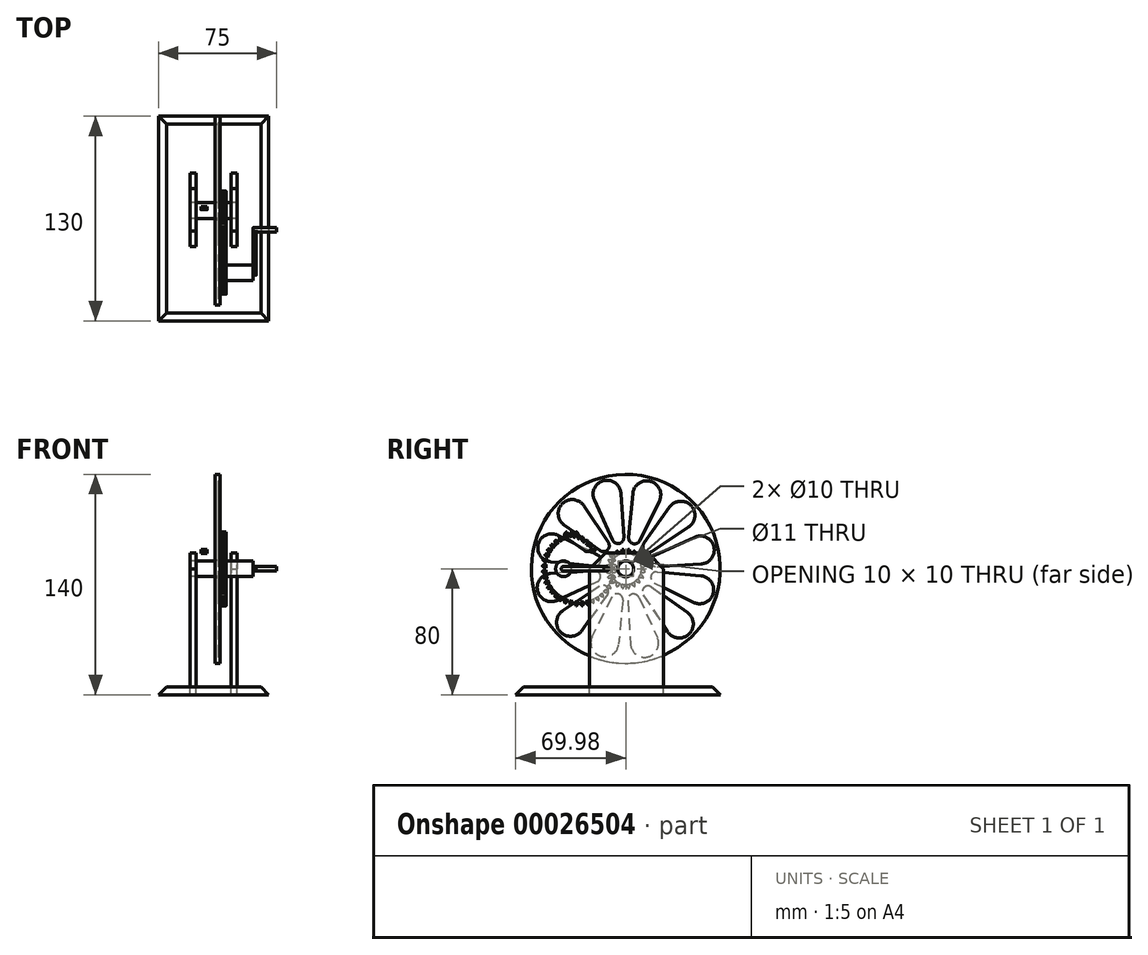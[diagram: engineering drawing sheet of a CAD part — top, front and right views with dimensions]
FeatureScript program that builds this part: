
annotation { "Feature Type Name" : "Feature", "Feature Type Description" : "" }
export const myFeature = defineFeature(function(context is Context, id is Id, definition is map)
    precondition{}
    {
        {
            var Q0;
            Q0=qCreatedBy(makeId("Right.planeOp"),FACE);
            var sketch = newSketch(context, id + "F0", { "sketchPlane" : qUnion([Q0])});
            skCircle(sketch, "E0", {"center": v(0, 0) * mm, "radius": 60 * mm});
            skLineSegment(sketch, "E1", {"start": v(1.87, 19.91) * mm, "end": v(4.48, 47.8) * mm});
            skLineSegment(sketch, "E2", {"start": v(8.88, 17.92) * mm, "end": v(21.32, 43) * mm});
            skCircle(sketch, "E3", {"center": v(0, 0) * mm, "radius": 5 * mm});
            skArc(sketch, "E4", {"start": v(1.87, 19.91) * mm, "mid": v(4.55, 16) * mm, "end": v(8.88, 17.92) * mm});
            skArc(sketch, "E5", {"start": v(4.48, 47.8) * mm, "mid": v(15.77, 55.52) * mm, "end": v(21.32, 43) * mm});
            skArc(sketch, "E6.1.0", {"start": v(-8.34, 18.18) * mm, "mid": v(-4.06, 16.13) * mm, "end": v(-1.27, 19.96) * mm});
            skArc(sketch, "E6.1.5", {"start": v(-20.01, 43.63) * mm, "mid": v(-14.1, 55.97) * mm, "end": v(-3.04, 47.9) * mm});
            skLineSegment(sketch, "E6.1.8", {"start": v(-1.27, 19.96) * mm, "end": v(-3.04, 47.9) * mm});
            skLineSegment(sketch, "E6.1.9", {"start": v(-8.34, 18.18) * mm, "end": v(-20.01, 43.63) * mm});
            skArc(sketch, "E6.2.0", {"start": v(-16.31, 11.57) * mm, "mid": v(-11.58, 11.94) * mm, "end": v(-11.08, 16.65) * mm});
            skArc(sketch, "E6.2.5", {"start": v(-39.15, 27.78) * mm, "mid": v(-40.2, 41.42) * mm, "end": v(-26.59, 39.96) * mm});
            skLineSegment(sketch, "E6.2.8", {"start": v(-11.08, 16.65) * mm, "end": v(-26.59, 39.96) * mm});
            skLineSegment(sketch, "E6.2.9", {"start": v(-16.31, 11.57) * mm, "end": v(-39.15, 27.78) * mm});
            skArc(sketch, "E6.3.0", {"start": v(-19.91, 1.87) * mm, "mid": v(-16, 4.55) * mm, "end": v(-17.92, 8.88) * mm});
            skArc(sketch, "E6.3.5", {"start": v(-47.8, 4.48) * mm, "mid": v(-55.52, 15.77) * mm, "end": v(-43, 21.32) * mm});
            skLineSegment(sketch, "E6.3.8", {"start": v(-17.92, 8.88) * mm, "end": v(-43, 21.32) * mm});
            skLineSegment(sketch, "E6.3.9", {"start": v(-19.91, 1.87) * mm, "end": v(-47.8, 4.48) * mm});
            skArc(sketch, "E6.4.0", {"start": v(-18.18, -8.34) * mm, "mid": v(-16.13, -4.06) * mm, "end": v(-19.96, -1.27) * mm});
            skArc(sketch, "E6.4.5", {"start": v(-43.63, -20.01) * mm, "mid": v(-55.97, -14.1) * mm, "end": v(-47.9, -3.04) * mm});
            skLineSegment(sketch, "E6.4.8", {"start": v(-19.96, -1.27) * mm, "end": v(-47.9, -3.04) * mm});
            skLineSegment(sketch, "E6.4.9", {"start": v(-18.18, -8.34) * mm, "end": v(-43.63, -20.01) * mm});
            skArc(sketch, "E6.5.0", {"start": v(-11.57, -16.31) * mm, "mid": v(-11.94, -11.58) * mm, "end": v(-16.65, -11.08) * mm});
            skArc(sketch, "E6.5.5", {"start": v(-27.78, -39.15) * mm, "mid": v(-41.42, -40.2) * mm, "end": v(-39.96, -26.59) * mm});
            skLineSegment(sketch, "E6.5.8", {"start": v(-16.65, -11.08) * mm, "end": v(-39.96, -26.59) * mm});
            skLineSegment(sketch, "E6.5.9", {"start": v(-11.57, -16.31) * mm, "end": v(-27.78, -39.15) * mm});
            skArc(sketch, "E6.6.0", {"start": v(-1.87, -19.91) * mm, "mid": v(-4.55, -16) * mm, "end": v(-8.88, -17.92) * mm});
            skArc(sketch, "E6.6.5", {"start": v(-4.48, -47.8) * mm, "mid": v(-15.77, -55.52) * mm, "end": v(-21.32, -43) * mm});
            skLineSegment(sketch, "E6.6.8", {"start": v(-8.88, -17.92) * mm, "end": v(-21.32, -43) * mm});
            skLineSegment(sketch, "E6.6.9", {"start": v(-1.87, -19.91) * mm, "end": v(-4.48, -47.8) * mm});
            skArc(sketch, "E6.7.0", {"start": v(8.34, -18.18) * mm, "mid": v(4.06, -16.13) * mm, "end": v(1.27, -19.96) * mm});
            skArc(sketch, "E6.7.5", {"start": v(20.01, -43.63) * mm, "mid": v(14.1, -55.97) * mm, "end": v(3.04, -47.9) * mm});
            skLineSegment(sketch, "E6.7.8", {"start": v(1.27, -19.96) * mm, "end": v(3.04, -47.9) * mm});
            skLineSegment(sketch, "E6.7.9", {"start": v(8.34, -18.18) * mm, "end": v(20.01, -43.63) * mm});
            skArc(sketch, "E6.8.0", {"start": v(16.31, -11.57) * mm, "mid": v(11.58, -11.94) * mm, "end": v(11.08, -16.65) * mm});
            skArc(sketch, "E6.8.5", {"start": v(39.15, -27.78) * mm, "mid": v(40.2, -41.42) * mm, "end": v(26.59, -39.96) * mm});
            skLineSegment(sketch, "E6.8.8", {"start": v(11.08, -16.65) * mm, "end": v(26.59, -39.96) * mm});
            skLineSegment(sketch, "E6.8.9", {"start": v(16.31, -11.57) * mm, "end": v(39.15, -27.78) * mm});
            skArc(sketch, "E6.9.0", {"start": v(19.91, -1.87) * mm, "mid": v(16, -4.55) * mm, "end": v(17.92, -8.88) * mm});
            skArc(sketch, "E6.9.5", {"start": v(47.8, -4.48) * mm, "mid": v(55.52, -15.77) * mm, "end": v(43, -21.32) * mm});
            skLineSegment(sketch, "E6.9.8", {"start": v(17.92, -8.88) * mm, "end": v(43, -21.32) * mm});
            skLineSegment(sketch, "E6.9.9", {"start": v(19.91, -1.87) * mm, "end": v(47.8, -4.48) * mm});
            skArc(sketch, "E6.10.0", {"start": v(18.18, 8.34) * mm, "mid": v(16.13, 4.06) * mm, "end": v(19.96, 1.27) * mm});
            skArc(sketch, "E6.10.5", {"start": v(43.63, 20.01) * mm, "mid": v(55.97, 14.1) * mm, "end": v(47.9, 3.04) * mm});
            skLineSegment(sketch, "E6.10.8", {"start": v(19.96, 1.27) * mm, "end": v(47.9, 3.04) * mm});
            skLineSegment(sketch, "E6.10.9", {"start": v(18.18, 8.34) * mm, "end": v(43.63, 20.01) * mm});
            skArc(sketch, "E6.11.0", {"start": v(11.57, 16.31) * mm, "mid": v(11.94, 11.58) * mm, "end": v(16.65, 11.08) * mm});
            skArc(sketch, "E6.11.5", {"start": v(27.78, 39.15) * mm, "mid": v(41.42, 40.2) * mm, "end": v(39.96, 26.59) * mm});
            skLineSegment(sketch, "E6.11.8", {"start": v(16.65, 11.08) * mm, "end": v(39.96, 26.59) * mm});
            skLineSegment(sketch, "E6.11.9", {"start": v(11.57, 16.31) * mm, "end": v(27.78, 39.15) * mm});
            skCircle(sketch, "E7", {"center": v(0, 0) * mm, "radius": 5.5 * mm});
            skSolve(sketch);
        }
        {
            var Q0;
            Q0=makeQuery(id+"F0.imprint","IMPRINT",FACE,{"disambiguationData":[TD([[makeQuery(id+"F0.imprint","IMPRINT",EDGE,{"derivedFrom":sQuery(id+"F0.wireOp",EDGE,"E0")}),1.0]])]});
            var Q1;
            Q1=makeQuery(id+"F0.imprint","IMPRINT",FACE,{"disambiguationData":[TD([[makeQuery(id+"F0.imprint","IMPRINT",EDGE,{"derivedFrom":sQuery(id+"F0.wireOp",EDGE,"E1")}),-1.0]])]});
            var Q2;
            Q2=makeQuery(id+"F0.imprint","IMPRINT",FACE,{"disambiguationData":[TD([[makeQuery(id+"F0.imprint","IMPRINT",EDGE,{"derivedFrom":sQuery(id+"F0.wireOp",EDGE,"E6.1.0")}),1.0]])]});
            var Q3;
            Q3=makeQuery(id+"F0.imprint","IMPRINT",FACE,{"disambiguationData":[TD([[makeQuery(id+"F0.imprint","IMPRINT",EDGE,{"derivedFrom":sQuery(id+"F0.wireOp",EDGE,"E6.2.0")}),1.0]])]});
            var Q4;
            Q4=makeQuery(id+"F0.imprint","IMPRINT",FACE,{"disambiguationData":[TD([[makeQuery(id+"F0.imprint","IMPRINT",EDGE,{"derivedFrom":sQuery(id+"F0.wireOp",EDGE,"E6.3.0")}),1.0]])]});
            var Q5;
            Q5=makeQuery(id+"F0.imprint","IMPRINT",FACE,{"disambiguationData":[TD([[makeQuery(id+"F0.imprint","IMPRINT",EDGE,{"derivedFrom":sQuery(id+"F0.wireOp",EDGE,"E6.4.0")}),1.0]])]});
            var Q6;
            Q6=makeQuery(id+"F0.imprint","IMPRINT",FACE,{"disambiguationData":[TD([[makeQuery(id+"F0.imprint","IMPRINT",EDGE,{"derivedFrom":sQuery(id+"F0.wireOp",EDGE,"E6.5.0")}),1.0]])]});
            var Q7;
            Q7=makeQuery(id+"F0.imprint","IMPRINT",FACE,{"disambiguationData":[TD([[makeQuery(id+"F0.imprint","IMPRINT",EDGE,{"derivedFrom":sQuery(id+"F0.wireOp",EDGE,"E6.6.0")}),1.0]])]});
            var Q8;
            Q8=makeQuery(id+"F0.imprint","IMPRINT",FACE,{"disambiguationData":[TD([[makeQuery(id+"F0.imprint","IMPRINT",EDGE,{"derivedFrom":sQuery(id+"F0.wireOp",EDGE,"E6.7.0")}),1.0]])]});
            var Q9;
            Q9=makeQuery(id+"F0.imprint","IMPRINT",FACE,{"disambiguationData":[TD([[makeQuery(id+"F0.imprint","IMPRINT",EDGE,{"derivedFrom":sQuery(id+"F0.wireOp",EDGE,"E6.8.0")}),1.0]])]});
            var Q10;
            Q10=makeQuery(id+"F0.imprint","IMPRINT",FACE,{"disambiguationData":[TD([[makeQuery(id+"F0.imprint","IMPRINT",EDGE,{"derivedFrom":sQuery(id+"F0.wireOp",EDGE,"E6.9.0")}),1.0]])]});
            var Q11;
            Q11=makeQuery(id+"F0.imprint","IMPRINT",FACE,{"disambiguationData":[TD([[makeQuery(id+"F0.imprint","IMPRINT",EDGE,{"derivedFrom":sQuery(id+"F0.wireOp",EDGE,"E6.10.0")}),1.0]])]});
            var Q12;
            Q12=makeQuery(id+"F0.imprint","IMPRINT",FACE,{"disambiguationData":[TD([[makeQuery(id+"F0.imprint","IMPRINT",EDGE,{"derivedFrom":sQuery(id+"F0.wireOp",EDGE,"E6.11.0")}),1.0]])]});
            var Q13;
            Q13=makeQuery(id+"F0.imprint","IMPRINT",FACE,{"disambiguationData":[TD([[makeQuery(id+"F0.imprint","IMPRINT",EDGE,{"derivedFrom":sQuery(id+"F0.wireOp",EDGE,"E3")}),1.0]])]});
            extrude(context, id + "F1", {"entities" : qUnion([Q0, Q1, Q2, Q3, Q4, Q5, Q6, Q7, Q8, Q9, Q10, Q11, Q12, Q13]), "oppositeDirection" : true, "depth" : 3 * mm});
        }
        {
            var Q0;
            Q0=makeQuery(id+"F0.imprint","IMPRINT",FACE,{"disambiguationData":[TD([[makeQuery(id+"F0.imprint","IMPRINT",EDGE,{"derivedFrom":sQuery(id+"F0.wireOp",EDGE,"E1")}),-1.0]])]});
            var Q1;
            Q1=makeQuery(id+"F0.imprint","IMPRINT",FACE,{"disambiguationData":[TD([[makeQuery(id+"F0.imprint","IMPRINT",EDGE,{"derivedFrom":sQuery(id+"F0.wireOp",EDGE,"E6.1.0")}),1.0]])]});
            var Q2;
            Q2=makeQuery(id+"F0.imprint","IMPRINT",FACE,{"disambiguationData":[TD([[makeQuery(id+"F0.imprint","IMPRINT",EDGE,{"derivedFrom":sQuery(id+"F0.wireOp",EDGE,"E6.2.0")}),1.0]])]});
            var Q3;
            Q3=makeQuery(id+"F0.imprint","IMPRINT",FACE,{"disambiguationData":[TD([[makeQuery(id+"F0.imprint","IMPRINT",EDGE,{"derivedFrom":sQuery(id+"F0.wireOp",EDGE,"E6.3.0")}),1.0]])]});
            var Q4;
            Q4=makeQuery(id+"F0.imprint","IMPRINT",FACE,{"disambiguationData":[TD([[makeQuery(id+"F0.imprint","IMPRINT",EDGE,{"derivedFrom":sQuery(id+"F0.wireOp",EDGE,"E6.4.0")}),1.0]])]});
            var Q5;
            Q5=makeQuery(id+"F0.imprint","IMPRINT",FACE,{"disambiguationData":[TD([[makeQuery(id+"F0.imprint","IMPRINT",EDGE,{"derivedFrom":sQuery(id+"F0.wireOp",EDGE,"E6.5.0")}),1.0]])]});
            var Q6;
            Q6=makeQuery(id+"F0.imprint","IMPRINT",FACE,{"disambiguationData":[TD([[makeQuery(id+"F0.imprint","IMPRINT",EDGE,{"derivedFrom":sQuery(id+"F0.wireOp",EDGE,"E6.6.0")}),1.0]])]});
            var Q7;
            Q7=makeQuery(id+"F0.imprint","IMPRINT",FACE,{"disambiguationData":[TD([[makeQuery(id+"F0.imprint","IMPRINT",EDGE,{"derivedFrom":sQuery(id+"F0.wireOp",EDGE,"E6.7.0")}),1.0]])]});
            var Q8;
            Q8=makeQuery(id+"F0.imprint","IMPRINT",FACE,{"disambiguationData":[TD([[makeQuery(id+"F0.imprint","IMPRINT",EDGE,{"derivedFrom":sQuery(id+"F0.wireOp",EDGE,"E6.8.0")}),1.0]])]});
            var Q9;
            Q9=makeQuery(id+"F0.imprint","IMPRINT",FACE,{"disambiguationData":[TD([[makeQuery(id+"F0.imprint","IMPRINT",EDGE,{"derivedFrom":sQuery(id+"F0.wireOp",EDGE,"E6.9.0")}),1.0]])]});
            var Q10;
            Q10=makeQuery(id+"F0.imprint","IMPRINT",FACE,{"disambiguationData":[TD([[makeQuery(id+"F0.imprint","IMPRINT",EDGE,{"derivedFrom":sQuery(id+"F0.wireOp",EDGE,"E6.10.0")}),1.0]])]});
            var Q11;
            Q11=makeQuery(id+"F0.imprint","IMPRINT",FACE,{"disambiguationData":[TD([[makeQuery(id+"F0.imprint","IMPRINT",EDGE,{"derivedFrom":sQuery(id+"F0.wireOp",EDGE,"E6.11.0")}),1.0]])]});
            extrude(context, id + "F2", {"entities" : qUnion([Q0, Q1, Q2, Q3, Q4, Q5, Q6, Q7, Q8, Q9, Q10, Q11]), "operationType" : NewBodyOperationType.REMOVE, "oppositeDirection" : true, "depth" : 1 * mm});
        }
        {
            var Q0;
            Q0=makeQuery(id+"F1.opExtrude","SWEPT_BODY",BODY,{"disambiguationData":[OSD([sQuery(id+"F0.wireOp",EDGE,"E3")])]});
            deleteBodies(context, id + "F3", {"entities" : qUnion([Q0])});
        }
        {
            var Q0;
            Q0=makeQuery(id+"F0.imprint","IMPRINT",FACE,{"disambiguationData":[TD([[makeQuery(id+"F0.imprint","IMPRINT",EDGE,{"derivedFrom":sQuery(id+"F0.wireOp",EDGE,"E3")}),1.0]])]});
            var Q1;
            Q1=sQuery(id+"F0.wireOp",EDGE,"E3");
            extrude(context, id + "F4", {"entities" : qUnion([Q0]), "surfaceEntities" : qUnion([Q1]), "endBound" : BoundingType.SYMMETRIC, "depth" : 30 * mm});
        }
        {
            var Q0;
            Q0=makeQuery(id+"F1.opExtrude","SWEPT_BODY",BODY,{"disambiguationData":[OSD([sQuery(id+"F0.wireOp",EDGE,"E0"),sQuery(id+"F0.wireOp",EDGE,"E7")])]});
            transform(context, id + "F5", {"entities" : qUnion([Q0]), "transformType" : TransformType.TRANSLATION_3D, "dx" : 4 * mm, "dy" : 0 * mm, "dz" : 0 * mm, "makeCopy" : false});
        }
        {
            var Q0;
            Q0=makeQuery(id+"F1.opExtrude","CAP_FACE",FACE,{"disambiguationData":[OSD([sQuery(id+"F0.wireOp",EDGE,"E0"),sQuery(id+"F0.wireOp",EDGE,"E7")])],"isStart":true});
            var sketch = newSketch(context, id + "F6", { "sketchPlane" : qUnion([Q0])});
            skCircle(sketch, "E8", {"center": v(0, 0) * mm, "radius": 5.5 * mm});
            skCircle(sketch, "E9", {"center": v(0, 0) * mm, "radius": 10 * mm});
            skCircle(sketch, "E10", {"center": v(0, 0) * mm, "radius": 11.25 * mm, "construction": true});
            skCircle(sketch, "E11", {"center": v(0, 0) * mm, "radius": 12.5 * mm, "construction": true});
            skLineSegment(sketch, "E12", {"start": v(0.88, 11.22) * mm, "end": v(5.26, 8.5) * mm, "construction": true});
            skLineSegment(sketch, "E13", {"start": v(0, 0) * mm, "end": v(0.98, 12.46) * mm, "construction": true});
            skArc(sketch, "E14", {"start": v(2.6, 10.94) * mm, "mid": v(1.75, 11.11) * mm, "end": v(0.88, 11.22) * mm, "construction": true});
            skFitSpline(sketch, "E15", {"points": [v(1.68, 12.39) * mm, v(0.88, 11.22) * mm, v(0.58, 9.98) * mm], "startDerivative": vector(-1.78, -2.2) * mm, "endDerivative": vector(-0.32, -2.61) * mm});
            skLineSegment(sketch, "E16", {"start": v(0.88, 11.22) * mm, "end": v(-2.32, 12.67) * mm, "construction": true});
            skLineSegment(sketch, "E17", {"start": v(0.88, 11.22) * mm, "end": v(-2.94, 11.52) * mm, "construction": true});
            skLineSegment(sketch, "E18", {"start": v(0, 0) * mm, "end": v(2.24, 14.13) * mm, "construction": true});
            skFitSpline(sketch, "E19.MirrorCS", {"points": [v(2.23, 12.3) * mm, v(2.63, 10.94) * mm, v(2.53, 9.67) * mm], "startDerivative": vector(1.01, -2.64) * mm, "endDerivative": vector(-0.5, -2.59) * mm});
            skArc(sketch, "E20", {"start": v(2.23, 12.3) * mm, "mid": v(1.96, 12.35) * mm, "end": v(1.68, 12.39) * mm});
            skSolve(sketch);
        }
        {
            var Q0;
            Q0=makeQuery(id+"F6.imprint","IMPRINT",FACE,{"disambiguationData":[TD([[makeQuery(id+"F6.imprint","IMPRINT",EDGE,{"derivedFrom":sQuery(id+"F6.wireOp",EDGE,"E8")}),-1.0]])]});
            extrude(context, id + "F7", {"entities" : qUnion([Q0]), "operationType" : NewBodyOperationType.ADD, "depth" : 4 * mm});
        }
        {
            var Q0;
            {var subQ1=sQuery(id+"F6.wireOp",EDGE,"E15");Q0=makeQuery(id+"F6.imprint","IMPRINT",FACE,{"disambiguationData":[TD([[makeQuery(id+"F6.imprint","IMPRINT",EDGE,{"derivedFrom":subQ1}),1.0]])]});}
            extrude(context, id + "F8", {"entities" : qUnion([Q0]), "depth" : 4 * mm});
        }
        {
            var Q0;
            Q0=makeQuery(id+"F8.opExtrude","SWEPT_BODY",BODY,{"disambiguationData":[OSD([sQuery(id+"F6.wireOp",EDGE,"E9"),sQuery(id+"F6.wireOp",EDGE,"E15"),sQuery(id+"F6.wireOp",EDGE,"E19.MirrorCS"),sQuery(id+"F6.wireOp",EDGE,"E20")])]});
            var Q1;
            Q1=makeQuery(id+"F7.opExtrude","CAP_EDGE",EDGE,{"disambiguationData":[OSD([sQuery(id+"F6.wireOp",EDGE,"E9")])],"isStart":false});
            circularPattern(context, id + "F9", {"entities" : qUnion([Q0]), "axis" : qUnion([Q1]), "angle" : 18 * degree, "instanceCount" : 20});
        }
        {
            var Q0;
            Q0=makeQuery(id+"F8.opExtrude","SWEPT_BODY",BODY,{"disambiguationData":[OSD([sQuery(id+"F6.wireOp",EDGE,"E9"),sQuery(id+"F6.wireOp",EDGE,"E15"),sQuery(id+"F6.wireOp",EDGE,"E19.MirrorCS"),sQuery(id+"F6.wireOp",EDGE,"E20")])]});
            var Q1;
            Q1=qCreatedBy(makeId("Right.planeOp"),FACE);
            mirror(context, id + "F10", {"entities" : qUnion([Q0]), "mirrorPlane" : qUnion([Q1])});
        }
        {
            var Q0;
            Q0=makeQuery(id+"F1.opExtrude","CAP_FACE",FACE,{"disambiguationData":[OSD([sQuery(id+"F0.wireOp",EDGE,"E0"),sQuery(id+"F0.wireOp",EDGE,"E7")])],"isStart":true});
            var sketch = newSketch(context, id + "F11", { "sketchPlane" : qUnion([Q0])});
            skCircle(sketch, "E21", {"center": v(-29.52, 0) * mm, "radius": 21.25 * mm});
            skCircle(sketch, "E22", {"center": v(-29.52, 0) * mm, "radius": 22.3 * mm, "construction": true});
            skCircle(sketch, "E23", {"center": v(-29.52, 0) * mm, "radius": 23.55 * mm, "construction": true});
            skLineSegment(sketch, "E24", {"start": v(-29.52, 0) * mm, "end": v(-29.52, 32.3) * mm, "construction": true});
            skLineSegment(sketch, "E25", {"start": v(-29.52, 0) * mm, "end": v(-28.3, 31.27) * mm, "construction": true});
            skLineSegment(sketch, "E26", {"start": v(-29.52, 0) * mm, "end": v(-25.78, 31.61) * mm, "construction": true});
            skArc(sketch, "E27", {"start": v(-26.9, 22.15) * mm, "mid": v(-27.77, 22.23) * mm, "end": v(-28.65, 22.28) * mm, "construction": true});
            skLineSegment(sketch, "E28", {"start": v(-28.65, 22.28) * mm, "end": v(-46.41, 29.55) * mm, "construction": true});
            skLineSegment(sketch, "E29", {"start": v(-28.65, 22.28) * mm, "end": v(-50.71, 23.15) * mm, "construction": true});
            skLineSegment(sketch, "E30", {"start": v(-29.52, 0) * mm, "end": v(-27.1, 30.68) * mm, "construction": true});
            skFitSpline(sketch, "E31", {"points": [v(-27.88, 23.5) * mm, v(-28.65, 22.28) * mm, v(-28.9, 21.24) * mm], "startDerivative": vector(-1.82, -2.16) * mm, "endDerivative": vector(-0.46, -2.6) * mm});
            skFitSpline(sketch, "E32.MirrorCS", {"points": [v(-27.47, 23.46) * mm, v(-26.9, 22.15) * mm, v(-26.82, 21.08) * mm], "startDerivative": vector(1.46, -2.42) * mm, "endDerivative": vector(0.05, -2.63) * mm});
            skArc(sketch, "E33", {"start": v(-27.47, 23.46) * mm, "mid": v(-27.68, 23.48) * mm, "end": v(-27.88, 23.5) * mm});
            skSolve(sketch);
        }
        {
            var Q0;
            {var subQ3=makeQuery(id+"F2.boolean.opBoolean","COPY",EDGE,{"derivedFrom":makeQuery(id+"F2.opExtrude","CAP_EDGE",EDGE,{"disambiguationData":[OSD([sQuery(id+"F0.wireOp",EDGE,"E6.3.0")])],"isStart":true})});Q0=makeQuery(id+"F11.imprint","IMPRINT",FACE,{"disambiguationData":[TD([[makeQuery(id+"F11.imprint","IMPRINT",EDGE,{"derivedFrom":subQ3}),1.0]])]});}
            var Q1;
            {var subQ1=sQuery(id+"F11.wireOp",EDGE,"E21");var subQ7=makeQuery(id+"F11.imprint","INTERSECT",VERTEX,{"derivedFrom":[subQ1,sQuery(id+"F11.wireOp",EDGE,"E32.MirrorCS")]});Q1=makeQuery(id+"F11.imprint","IMPRINT",FACE,{"disambiguationData":[TD([[makeQuery(id+"F11.imprint","IMPRINT",EDGE,{"disambiguationData":[TD([[subQ7,1.0]])],"derivedFrom":subQ1}),1.0]])]});}
            var Q2;
            {var subQ0=sQuery(id+"F6.wireOp",EDGE,"E15");var subQ1=makeQuery(id+"F8.opExtrude","CAP_EDGE",EDGE,{"disambiguationData":[OSD([subQ0])],"isStart":true});Q2=makeQuery(id+"F11.imprint","IMPRINT",FACE,{"disambiguationData":[TD([[makeQuery(id+"F11.imprint","IMPRINT",EDGE,{"derivedFrom":makeQuery(id+"F9.opPattern","COPY",EDGE,{"derivedFrom":subQ1,"instanceName":"4"})}),1.0]])]});}
            var Q3;
            {var subQ4=makeQuery(id+"F2.boolean.opBoolean","COPY",EDGE,{"derivedFrom":makeQuery(id+"F2.opExtrude","CAP_EDGE",EDGE,{"disambiguationData":[OSD([sQuery(id+"F0.wireOp",EDGE,"E6.4.0")])],"isStart":true})});Q3=makeQuery(id+"F11.imprint","IMPRINT",FACE,{"disambiguationData":[TD([[makeQuery(id+"F11.imprint","IMPRINT",EDGE,{"derivedFrom":subQ4}),1.0]])]});}
            var Q4;
            {var subQ10=makeQuery(id+"F2.boolean.opBoolean","COPY",EDGE,{"derivedFrom":makeQuery(id+"F2.opExtrude","CAP_EDGE",EDGE,{"disambiguationData":[OSD([sQuery(id+"F0.wireOp",EDGE,"E6.3.0")])],"isStart":true})});Q4=makeQuery(id+"F11.imprint","IMPRINT",FACE,{"disambiguationData":[TD([[makeQuery(id+"F11.imprint","IMPRINT",EDGE,{"derivedFrom":subQ10}),-1.0]])]});}
            var Q5;
            {var subQ0=makeQuery(id+"F2.boolean.opBoolean","COPY",EDGE,{"derivedFrom":makeQuery(id+"F2.opExtrude","CAP_EDGE",EDGE,{"disambiguationData":[OSD([sQuery(id+"F0.wireOp",EDGE,"E6.5.8")])],"isStart":true})});var subQ1=sQuery(id+"F11.wireOp",EDGE,"E21");var subQ2=makeQuery(id+"F11.imprint","INTERSECT",VERTEX,{"derivedFrom":[subQ0,subQ1]});Q5=makeQuery(id+"F11.imprint","IMPRINT",FACE,{"disambiguationData":[TD([[makeQuery(id+"F11.imprint","IMPRINT",EDGE,{"disambiguationData":[TD([[subQ2,-1.0]])],"derivedFrom":subQ1}),1.0]])]});}
            extrude(context, id + "F12", {"entities" : qUnion([Q0, Q1, Q2, Q3, Q4, Q5]), "depth" : 4 * mm});
        }
        {
            var Q0;
            {var subQ1=sQuery(id+"F11.wireOp",EDGE,"E31");Q0=makeQuery(id+"F11.imprint","IMPRINT",FACE,{"disambiguationData":[TD([[makeQuery(id+"F11.imprint","IMPRINT",EDGE,{"derivedFrom":subQ1}),1.0]])]});}
            extrude(context, id + "F13", {"entities" : qUnion([Q0]), "depth" : 4 * mm});
        }
        {
            var Q0;
            Q0=makeQuery(id+"F13.opExtrude","SWEPT_BODY",BODY,{"disambiguationData":[OSD([sQuery(id+"F11.wireOp",EDGE,"E21"),sQuery(id+"F11.wireOp",EDGE,"E31"),sQuery(id+"F11.wireOp",EDGE,"E32.MirrorCS"),sQuery(id+"F11.wireOp",EDGE,"E33")])]});
            var Q1;
            Q1=makeQuery(id+"F12.opExtrude","CAP_EDGE",EDGE,{"disambiguationData":[OSD([sQuery(id+"F11.wireOp",EDGE,"E21")])],"isStart":false});
            circularPattern(context, id + "F14", {"entities" : qUnion([Q0]), "axis" : qUnion([Q1]), "angle" : 9 * degree, "instanceCount" : 40});
        }
        {
            var Q0;
            Q0=makeQuery(id+"F12.opExtrude","SWEPT_BODY",BODY,{"disambiguationData":[OSD([sQuery(id+"F11.wireOp",EDGE,"E21")])]});
            var Q1;
            Q1=makeQuery(id+"F13.opExtrude","SWEPT_BODY",BODY,{"disambiguationData":[OSD([sQuery(id+"F11.wireOp",EDGE,"E21"),sQuery(id+"F11.wireOp",EDGE,"E31"),sQuery(id+"F11.wireOp",EDGE,"E32.MirrorCS"),sQuery(id+"F11.wireOp",EDGE,"E33")])]});
            var Q2;
            Q2=makeQuery(id+"F14.opPattern","COPY",BODY,{"derivedFrom":makeQuery(id+"F13.opExtrude","SWEPT_BODY",BODY,{"disambiguationData":[OSD([sQuery(id+"F11.wireOp",EDGE,"E21"),sQuery(id+"F11.wireOp",EDGE,"E31"),sQuery(id+"F11.wireOp",EDGE,"E32.MirrorCS"),sQuery(id+"F11.wireOp",EDGE,"E33")])]}),"instanceName":"1"});
            var Q3;
            Q3=makeQuery(id+"F14.opPattern","COPY",BODY,{"derivedFrom":makeQuery(id+"F13.opExtrude","SWEPT_BODY",BODY,{"disambiguationData":[OSD([sQuery(id+"F11.wireOp",EDGE,"E21"),sQuery(id+"F11.wireOp",EDGE,"E31"),sQuery(id+"F11.wireOp",EDGE,"E32.MirrorCS"),sQuery(id+"F11.wireOp",EDGE,"E33")])]}),"instanceName":"2"});
            var Q4;
            Q4=makeQuery(id+"F14.opPattern","COPY",BODY,{"derivedFrom":makeQuery(id+"F13.opExtrude","SWEPT_BODY",BODY,{"disambiguationData":[OSD([sQuery(id+"F11.wireOp",EDGE,"E21"),sQuery(id+"F11.wireOp",EDGE,"E31"),sQuery(id+"F11.wireOp",EDGE,"E32.MirrorCS"),sQuery(id+"F11.wireOp",EDGE,"E33")])]}),"instanceName":"3"});
            var Q5;
            Q5=makeQuery(id+"F14.opPattern","COPY",BODY,{"derivedFrom":makeQuery(id+"F13.opExtrude","SWEPT_BODY",BODY,{"disambiguationData":[OSD([sQuery(id+"F11.wireOp",EDGE,"E21"),sQuery(id+"F11.wireOp",EDGE,"E31"),sQuery(id+"F11.wireOp",EDGE,"E32.MirrorCS"),sQuery(id+"F11.wireOp",EDGE,"E33")])]}),"instanceName":"4"});
            var Q6;
            Q6=makeQuery(id+"F14.opPattern","COPY",BODY,{"derivedFrom":makeQuery(id+"F13.opExtrude","SWEPT_BODY",BODY,{"disambiguationData":[OSD([sQuery(id+"F11.wireOp",EDGE,"E21"),sQuery(id+"F11.wireOp",EDGE,"E31"),sQuery(id+"F11.wireOp",EDGE,"E32.MirrorCS"),sQuery(id+"F11.wireOp",EDGE,"E33")])]}),"instanceName":"5"});
            var Q7;
            Q7=makeQuery(id+"F14.opPattern","COPY",BODY,{"derivedFrom":makeQuery(id+"F13.opExtrude","SWEPT_BODY",BODY,{"disambiguationData":[OSD([sQuery(id+"F11.wireOp",EDGE,"E21"),sQuery(id+"F11.wireOp",EDGE,"E31"),sQuery(id+"F11.wireOp",EDGE,"E32.MirrorCS"),sQuery(id+"F11.wireOp",EDGE,"E33")])]}),"instanceName":"6"});
            var Q8;
            Q8=makeQuery(id+"F14.opPattern","COPY",BODY,{"derivedFrom":makeQuery(id+"F13.opExtrude","SWEPT_BODY",BODY,{"disambiguationData":[OSD([sQuery(id+"F11.wireOp",EDGE,"E21"),sQuery(id+"F11.wireOp",EDGE,"E31"),sQuery(id+"F11.wireOp",EDGE,"E32.MirrorCS"),sQuery(id+"F11.wireOp",EDGE,"E33")])]}),"instanceName":"7"});
            var Q9;
            Q9=makeQuery(id+"F14.opPattern","COPY",BODY,{"derivedFrom":makeQuery(id+"F13.opExtrude","SWEPT_BODY",BODY,{"disambiguationData":[OSD([sQuery(id+"F11.wireOp",EDGE,"E21"),sQuery(id+"F11.wireOp",EDGE,"E31"),sQuery(id+"F11.wireOp",EDGE,"E32.MirrorCS"),sQuery(id+"F11.wireOp",EDGE,"E33")])]}),"instanceName":"8"});
            var Q10;
            Q10=makeQuery(id+"F14.opPattern","COPY",BODY,{"derivedFrom":makeQuery(id+"F13.opExtrude","SWEPT_BODY",BODY,{"disambiguationData":[OSD([sQuery(id+"F11.wireOp",EDGE,"E21"),sQuery(id+"F11.wireOp",EDGE,"E31"),sQuery(id+"F11.wireOp",EDGE,"E32.MirrorCS"),sQuery(id+"F11.wireOp",EDGE,"E33")])]}),"instanceName":"9"});
            var Q11;
            Q11=makeQuery(id+"F14.opPattern","COPY",BODY,{"derivedFrom":makeQuery(id+"F13.opExtrude","SWEPT_BODY",BODY,{"disambiguationData":[OSD([sQuery(id+"F11.wireOp",EDGE,"E21"),sQuery(id+"F11.wireOp",EDGE,"E31"),sQuery(id+"F11.wireOp",EDGE,"E32.MirrorCS"),sQuery(id+"F11.wireOp",EDGE,"E33")])]}),"instanceName":"10"});
            var Q12;
            Q12=makeQuery(id+"F14.opPattern","COPY",BODY,{"derivedFrom":makeQuery(id+"F13.opExtrude","SWEPT_BODY",BODY,{"disambiguationData":[OSD([sQuery(id+"F11.wireOp",EDGE,"E21"),sQuery(id+"F11.wireOp",EDGE,"E31"),sQuery(id+"F11.wireOp",EDGE,"E32.MirrorCS"),sQuery(id+"F11.wireOp",EDGE,"E33")])]}),"instanceName":"11"});
            var Q13;
            Q13=makeQuery(id+"F14.opPattern","COPY",BODY,{"derivedFrom":makeQuery(id+"F13.opExtrude","SWEPT_BODY",BODY,{"disambiguationData":[OSD([sQuery(id+"F11.wireOp",EDGE,"E21"),sQuery(id+"F11.wireOp",EDGE,"E31"),sQuery(id+"F11.wireOp",EDGE,"E32.MirrorCS"),sQuery(id+"F11.wireOp",EDGE,"E33")])]}),"instanceName":"12"});
            var Q14;
            Q14=makeQuery(id+"F14.opPattern","COPY",BODY,{"derivedFrom":makeQuery(id+"F13.opExtrude","SWEPT_BODY",BODY,{"disambiguationData":[OSD([sQuery(id+"F11.wireOp",EDGE,"E21"),sQuery(id+"F11.wireOp",EDGE,"E31"),sQuery(id+"F11.wireOp",EDGE,"E32.MirrorCS"),sQuery(id+"F11.wireOp",EDGE,"E33")])]}),"instanceName":"13"});
            var Q15;
            Q15=makeQuery(id+"F14.opPattern","COPY",BODY,{"derivedFrom":makeQuery(id+"F13.opExtrude","SWEPT_BODY",BODY,{"disambiguationData":[OSD([sQuery(id+"F11.wireOp",EDGE,"E21"),sQuery(id+"F11.wireOp",EDGE,"E31"),sQuery(id+"F11.wireOp",EDGE,"E32.MirrorCS"),sQuery(id+"F11.wireOp",EDGE,"E33")])]}),"instanceName":"14"});
            var Q16;
            Q16=makeQuery(id+"F14.opPattern","COPY",BODY,{"derivedFrom":makeQuery(id+"F13.opExtrude","SWEPT_BODY",BODY,{"disambiguationData":[OSD([sQuery(id+"F11.wireOp",EDGE,"E21"),sQuery(id+"F11.wireOp",EDGE,"E31"),sQuery(id+"F11.wireOp",EDGE,"E32.MirrorCS"),sQuery(id+"F11.wireOp",EDGE,"E33")])]}),"instanceName":"15"});
            var Q17;
            Q17=makeQuery(id+"F14.opPattern","COPY",BODY,{"derivedFrom":makeQuery(id+"F13.opExtrude","SWEPT_BODY",BODY,{"disambiguationData":[OSD([sQuery(id+"F11.wireOp",EDGE,"E21"),sQuery(id+"F11.wireOp",EDGE,"E31"),sQuery(id+"F11.wireOp",EDGE,"E32.MirrorCS"),sQuery(id+"F11.wireOp",EDGE,"E33")])]}),"instanceName":"16"});
            var Q18;
            Q18=makeQuery(id+"F14.opPattern","COPY",BODY,{"derivedFrom":makeQuery(id+"F13.opExtrude","SWEPT_BODY",BODY,{"disambiguationData":[OSD([sQuery(id+"F11.wireOp",EDGE,"E21"),sQuery(id+"F11.wireOp",EDGE,"E31"),sQuery(id+"F11.wireOp",EDGE,"E32.MirrorCS"),sQuery(id+"F11.wireOp",EDGE,"E33")])]}),"instanceName":"17"});
            var Q19;
            Q19=makeQuery(id+"F14.opPattern","COPY",BODY,{"derivedFrom":makeQuery(id+"F13.opExtrude","SWEPT_BODY",BODY,{"disambiguationData":[OSD([sQuery(id+"F11.wireOp",EDGE,"E21"),sQuery(id+"F11.wireOp",EDGE,"E31"),sQuery(id+"F11.wireOp",EDGE,"E32.MirrorCS"),sQuery(id+"F11.wireOp",EDGE,"E33")])]}),"instanceName":"18"});
            var Q20;
            Q20=makeQuery(id+"F14.opPattern","COPY",BODY,{"derivedFrom":makeQuery(id+"F13.opExtrude","SWEPT_BODY",BODY,{"disambiguationData":[OSD([sQuery(id+"F11.wireOp",EDGE,"E21"),sQuery(id+"F11.wireOp",EDGE,"E31"),sQuery(id+"F11.wireOp",EDGE,"E32.MirrorCS"),sQuery(id+"F11.wireOp",EDGE,"E33")])]}),"instanceName":"19"});
            var Q21;
            Q21=makeQuery(id+"F14.opPattern","COPY",BODY,{"derivedFrom":makeQuery(id+"F13.opExtrude","SWEPT_BODY",BODY,{"disambiguationData":[OSD([sQuery(id+"F11.wireOp",EDGE,"E21"),sQuery(id+"F11.wireOp",EDGE,"E31"),sQuery(id+"F11.wireOp",EDGE,"E32.MirrorCS"),sQuery(id+"F11.wireOp",EDGE,"E33")])]}),"instanceName":"20"});
            var Q22;
            Q22=makeQuery(id+"F14.opPattern","COPY",BODY,{"derivedFrom":makeQuery(id+"F13.opExtrude","SWEPT_BODY",BODY,{"disambiguationData":[OSD([sQuery(id+"F11.wireOp",EDGE,"E21"),sQuery(id+"F11.wireOp",EDGE,"E31"),sQuery(id+"F11.wireOp",EDGE,"E32.MirrorCS"),sQuery(id+"F11.wireOp",EDGE,"E33")])]}),"instanceName":"21"});
            var Q23;
            Q23=makeQuery(id+"F14.opPattern","COPY",BODY,{"derivedFrom":makeQuery(id+"F13.opExtrude","SWEPT_BODY",BODY,{"disambiguationData":[OSD([sQuery(id+"F11.wireOp",EDGE,"E21"),sQuery(id+"F11.wireOp",EDGE,"E31"),sQuery(id+"F11.wireOp",EDGE,"E32.MirrorCS"),sQuery(id+"F11.wireOp",EDGE,"E33")])]}),"instanceName":"22"});
            var Q24;
            Q24=makeQuery(id+"F14.opPattern","COPY",BODY,{"derivedFrom":makeQuery(id+"F13.opExtrude","SWEPT_BODY",BODY,{"disambiguationData":[OSD([sQuery(id+"F11.wireOp",EDGE,"E21"),sQuery(id+"F11.wireOp",EDGE,"E31"),sQuery(id+"F11.wireOp",EDGE,"E32.MirrorCS"),sQuery(id+"F11.wireOp",EDGE,"E33")])]}),"instanceName":"23"});
            var Q25;
            Q25=makeQuery(id+"F14.opPattern","COPY",BODY,{"derivedFrom":makeQuery(id+"F13.opExtrude","SWEPT_BODY",BODY,{"disambiguationData":[OSD([sQuery(id+"F11.wireOp",EDGE,"E21"),sQuery(id+"F11.wireOp",EDGE,"E31"),sQuery(id+"F11.wireOp",EDGE,"E32.MirrorCS"),sQuery(id+"F11.wireOp",EDGE,"E33")])]}),"instanceName":"24"});
            var Q26;
            Q26=makeQuery(id+"F14.opPattern","COPY",BODY,{"derivedFrom":makeQuery(id+"F13.opExtrude","SWEPT_BODY",BODY,{"disambiguationData":[OSD([sQuery(id+"F11.wireOp",EDGE,"E21"),sQuery(id+"F11.wireOp",EDGE,"E31"),sQuery(id+"F11.wireOp",EDGE,"E32.MirrorCS"),sQuery(id+"F11.wireOp",EDGE,"E33")])]}),"instanceName":"25"});
            var Q27;
            Q27=makeQuery(id+"F14.opPattern","COPY",BODY,{"derivedFrom":makeQuery(id+"F13.opExtrude","SWEPT_BODY",BODY,{"disambiguationData":[OSD([sQuery(id+"F11.wireOp",EDGE,"E21"),sQuery(id+"F11.wireOp",EDGE,"E31"),sQuery(id+"F11.wireOp",EDGE,"E32.MirrorCS"),sQuery(id+"F11.wireOp",EDGE,"E33")])]}),"instanceName":"26"});
            var Q28;
            Q28=makeQuery(id+"F14.opPattern","COPY",BODY,{"derivedFrom":makeQuery(id+"F13.opExtrude","SWEPT_BODY",BODY,{"disambiguationData":[OSD([sQuery(id+"F11.wireOp",EDGE,"E21"),sQuery(id+"F11.wireOp",EDGE,"E31"),sQuery(id+"F11.wireOp",EDGE,"E32.MirrorCS"),sQuery(id+"F11.wireOp",EDGE,"E33")])]}),"instanceName":"27"});
            var Q29;
            Q29=makeQuery(id+"F14.opPattern","COPY",BODY,{"derivedFrom":makeQuery(id+"F13.opExtrude","SWEPT_BODY",BODY,{"disambiguationData":[OSD([sQuery(id+"F11.wireOp",EDGE,"E21"),sQuery(id+"F11.wireOp",EDGE,"E31"),sQuery(id+"F11.wireOp",EDGE,"E32.MirrorCS"),sQuery(id+"F11.wireOp",EDGE,"E33")])]}),"instanceName":"28"});
            var Q30;
            Q30=makeQuery(id+"F14.opPattern","COPY",BODY,{"derivedFrom":makeQuery(id+"F13.opExtrude","SWEPT_BODY",BODY,{"disambiguationData":[OSD([sQuery(id+"F11.wireOp",EDGE,"E21"),sQuery(id+"F11.wireOp",EDGE,"E31"),sQuery(id+"F11.wireOp",EDGE,"E32.MirrorCS"),sQuery(id+"F11.wireOp",EDGE,"E33")])]}),"instanceName":"29"});
            var Q31;
            Q31=makeQuery(id+"F14.opPattern","COPY",BODY,{"derivedFrom":makeQuery(id+"F13.opExtrude","SWEPT_BODY",BODY,{"disambiguationData":[OSD([sQuery(id+"F11.wireOp",EDGE,"E21"),sQuery(id+"F11.wireOp",EDGE,"E31"),sQuery(id+"F11.wireOp",EDGE,"E32.MirrorCS"),sQuery(id+"F11.wireOp",EDGE,"E33")])]}),"instanceName":"30"});
            var Q32;
            Q32=makeQuery(id+"F14.opPattern","COPY",BODY,{"derivedFrom":makeQuery(id+"F13.opExtrude","SWEPT_BODY",BODY,{"disambiguationData":[OSD([sQuery(id+"F11.wireOp",EDGE,"E21"),sQuery(id+"F11.wireOp",EDGE,"E31"),sQuery(id+"F11.wireOp",EDGE,"E32.MirrorCS"),sQuery(id+"F11.wireOp",EDGE,"E33")])]}),"instanceName":"31"});
            var Q33;
            Q33=makeQuery(id+"F14.opPattern","COPY",BODY,{"derivedFrom":makeQuery(id+"F13.opExtrude","SWEPT_BODY",BODY,{"disambiguationData":[OSD([sQuery(id+"F11.wireOp",EDGE,"E21"),sQuery(id+"F11.wireOp",EDGE,"E31"),sQuery(id+"F11.wireOp",EDGE,"E32.MirrorCS"),sQuery(id+"F11.wireOp",EDGE,"E33")])]}),"instanceName":"32"});
            var Q34;
            Q34=makeQuery(id+"F14.opPattern","COPY",BODY,{"derivedFrom":makeQuery(id+"F13.opExtrude","SWEPT_BODY",BODY,{"disambiguationData":[OSD([sQuery(id+"F11.wireOp",EDGE,"E21"),sQuery(id+"F11.wireOp",EDGE,"E31"),sQuery(id+"F11.wireOp",EDGE,"E32.MirrorCS"),sQuery(id+"F11.wireOp",EDGE,"E33")])]}),"instanceName":"33"});
            var Q35;
            Q35=makeQuery(id+"F14.opPattern","COPY",BODY,{"derivedFrom":makeQuery(id+"F13.opExtrude","SWEPT_BODY",BODY,{"disambiguationData":[OSD([sQuery(id+"F11.wireOp",EDGE,"E21"),sQuery(id+"F11.wireOp",EDGE,"E31"),sQuery(id+"F11.wireOp",EDGE,"E32.MirrorCS"),sQuery(id+"F11.wireOp",EDGE,"E33")])]}),"instanceName":"34"});
            var Q36;
            Q36=makeQuery(id+"F14.opPattern","COPY",BODY,{"derivedFrom":makeQuery(id+"F13.opExtrude","SWEPT_BODY",BODY,{"disambiguationData":[OSD([sQuery(id+"F11.wireOp",EDGE,"E21"),sQuery(id+"F11.wireOp",EDGE,"E31"),sQuery(id+"F11.wireOp",EDGE,"E32.MirrorCS"),sQuery(id+"F11.wireOp",EDGE,"E33")])]}),"instanceName":"35"});
            var Q37;
            Q37=makeQuery(id+"F14.opPattern","COPY",BODY,{"derivedFrom":makeQuery(id+"F13.opExtrude","SWEPT_BODY",BODY,{"disambiguationData":[OSD([sQuery(id+"F11.wireOp",EDGE,"E21"),sQuery(id+"F11.wireOp",EDGE,"E31"),sQuery(id+"F11.wireOp",EDGE,"E32.MirrorCS"),sQuery(id+"F11.wireOp",EDGE,"E33")])]}),"instanceName":"36"});
            var Q38;
            Q38=makeQuery(id+"F14.opPattern","COPY",BODY,{"derivedFrom":makeQuery(id+"F13.opExtrude","SWEPT_BODY",BODY,{"disambiguationData":[OSD([sQuery(id+"F11.wireOp",EDGE,"E21"),sQuery(id+"F11.wireOp",EDGE,"E31"),sQuery(id+"F11.wireOp",EDGE,"E32.MirrorCS"),sQuery(id+"F11.wireOp",EDGE,"E33")])]}),"instanceName":"37"});
            var Q39;
            Q39=makeQuery(id+"F14.opPattern","COPY",BODY,{"derivedFrom":makeQuery(id+"F13.opExtrude","SWEPT_BODY",BODY,{"disambiguationData":[OSD([sQuery(id+"F11.wireOp",EDGE,"E21"),sQuery(id+"F11.wireOp",EDGE,"E31"),sQuery(id+"F11.wireOp",EDGE,"E32.MirrorCS"),sQuery(id+"F11.wireOp",EDGE,"E33")])]}),"instanceName":"38"});
            var Q40;
            Q40=makeQuery(id+"F14.opPattern","COPY",BODY,{"derivedFrom":makeQuery(id+"F13.opExtrude","SWEPT_BODY",BODY,{"disambiguationData":[OSD([sQuery(id+"F11.wireOp",EDGE,"E21"),sQuery(id+"F11.wireOp",EDGE,"E31"),sQuery(id+"F11.wireOp",EDGE,"E32.MirrorCS"),sQuery(id+"F11.wireOp",EDGE,"E33")])]}),"instanceName":"39"});
            booleanBodies(context, id + "F15", {"operationType" : BooleanOperationType.UNION, "tools" : qUnion([Q0, Q1, Q2, Q3, Q4, Q5, Q6, Q7, Q8, Q9, Q10, Q11, Q12, Q13, Q14, Q15, Q16, Q17, Q18, Q19, Q20, Q21, Q22, Q23, Q24, Q25, Q26, Q27, Q28, Q29, Q30, Q31, Q32, Q33, Q34, Q35, Q36, Q37, Q38, Q39, Q40])});
        }
        {
            var Q0;
            Q0=makeQuery(id+"F12.opExtrude","SWEPT_BODY",BODY,{"disambiguationData":[OSD([sQuery(id+"F11.wireOp",EDGE,"E21")])]});
            transform(context, id + "F16", {"entities" : qUnion([Q0]), "transformType" : TransformType.TRANSLATION_3D, "dx" : 0 * mm, "dy" : -10 * mm, "dz" : 0 * mm, "makeCopy" : false});
        }
        {
            var Q0;
            {var subQ0=sQuery(id+"F11.wireOp",EDGE,"E21");var subQ1=makeQuery(id+"F13.opExtrude","CAP_FACE",FACE,{"disambiguationData":[OSD([subQ0,sQuery(id+"F11.wireOp",EDGE,"E31"),sQuery(id+"F11.wireOp",EDGE,"E32.MirrorCS"),sQuery(id+"F11.wireOp",EDGE,"E33")])],"isStart":false});Q0=makeQuery(id+"F15.opBoolean","MERGE",FACE,{"derivedFrom":[makeQuery(id+"F12.opExtrude","CAP_FACE",FACE,{"disambiguationData":[OSD([subQ0])],"isStart":false}),subQ1,makeQuery(id+"F14.opPattern","COPY",FACE,{"derivedFrom":subQ1,"instanceName":"1"}),makeQuery(id+"F14.opPattern","COPY",FACE,{"derivedFrom":subQ1,"instanceName":"2"}),makeQuery(id+"F14.opPattern","COPY",FACE,{"derivedFrom":subQ1,"instanceName":"3"}),makeQuery(id+"F14.opPattern","COPY",FACE,{"derivedFrom":subQ1,"instanceName":"4"}),makeQuery(id+"F14.opPattern","COPY",FACE,{"derivedFrom":subQ1,"instanceName":"5"}),makeQuery(id+"F14.opPattern","COPY",FACE,{"derivedFrom":subQ1,"instanceName":"6"}),makeQuery(id+"F14.opPattern","COPY",FACE,{"derivedFrom":subQ1,"instanceName":"7"}),makeQuery(id+"F14.opPattern","COPY",FACE,{"derivedFrom":subQ1,"instanceName":"8"}),makeQuery(id+"F14.opPattern","COPY",FACE,{"derivedFrom":subQ1,"instanceName":"9"}),makeQuery(id+"F14.opPattern","COPY",FACE,{"derivedFrom":subQ1,"instanceName":"10"}),makeQuery(id+"F14.opPattern","COPY",FACE,{"derivedFrom":subQ1,"instanceName":"11"}),makeQuery(id+"F14.opPattern","COPY",FACE,{"derivedFrom":subQ1,"instanceName":"12"}),makeQuery(id+"F14.opPattern","COPY",FACE,{"derivedFrom":subQ1,"instanceName":"13"}),makeQuery(id+"F14.opPattern","COPY",FACE,{"derivedFrom":subQ1,"instanceName":"14"}),makeQuery(id+"F14.opPattern","COPY",FACE,{"derivedFrom":subQ1,"instanceName":"15"}),makeQuery(id+"F14.opPattern","COPY",FACE,{"derivedFrom":subQ1,"instanceName":"16"}),makeQuery(id+"F14.opPattern","COPY",FACE,{"derivedFrom":subQ1,"instanceName":"17"}),makeQuery(id+"F14.opPattern","COPY",FACE,{"derivedFrom":subQ1,"instanceName":"18"}),makeQuery(id+"F14.opPattern","COPY",FACE,{"derivedFrom":subQ1,"instanceName":"19"}),makeQuery(id+"F14.opPattern","COPY",FACE,{"derivedFrom":subQ1,"instanceName":"20"}),makeQuery(id+"F14.opPattern","COPY",FACE,{"derivedFrom":subQ1,"instanceName":"21"}),makeQuery(id+"F14.opPattern","COPY",FACE,{"derivedFrom":subQ1,"instanceName":"22"}),makeQuery(id+"F14.opPattern","COPY",FACE,{"derivedFrom":subQ1,"instanceName":"23"}),makeQuery(id+"F14.opPattern","COPY",FACE,{"derivedFrom":subQ1,"instanceName":"24"}),makeQuery(id+"F14.opPattern","COPY",FACE,{"derivedFrom":subQ1,"instanceName":"25"}),makeQuery(id+"F14.opPattern","COPY",FACE,{"derivedFrom":subQ1,"instanceName":"26"}),makeQuery(id+"F14.opPattern","COPY",FACE,{"derivedFrom":subQ1,"instanceName":"27"}),makeQuery(id+"F14.opPattern","COPY",FACE,{"derivedFrom":subQ1,"instanceName":"28"}),makeQuery(id+"F14.opPattern","COPY",FACE,{"derivedFrom":subQ1,"instanceName":"29"}),makeQuery(id+"F14.opPattern","COPY",FACE,{"derivedFrom":subQ1,"instanceName":"30"}),makeQuery(id+"F14.opPattern","COPY",FACE,{"derivedFrom":subQ1,"instanceName":"31"}),makeQuery(id+"F14.opPattern","COPY",FACE,{"derivedFrom":subQ1,"instanceName":"32"}),makeQuery(id+"F14.opPattern","COPY",FACE,{"derivedFrom":subQ1,"instanceName":"33"}),makeQuery(id+"F14.opPattern","COPY",FACE,{"derivedFrom":subQ1,"instanceName":"34"}),makeQuery(id+"F14.opPattern","COPY",FACE,{"derivedFrom":subQ1,"instanceName":"35"}),makeQuery(id+"F14.opPattern","COPY",FACE,{"derivedFrom":subQ1,"instanceName":"36"}),makeQuery(id+"F14.opPattern","COPY",FACE,{"derivedFrom":subQ1,"instanceName":"37"}),makeQuery(id+"F14.opPattern","COPY",FACE,{"derivedFrom":subQ1,"instanceName":"38"}),makeQuery(id+"F14.opPattern","COPY",FACE,{"derivedFrom":subQ1,"instanceName":"39"})]});}
            var sketch = newSketch(context, id + "F17", { "sketchPlane" : qUnion([Q0])});
            skCircle(sketch, "E34", {"center": v(-39.52, 0) * mm, "radius": 5 * mm});
            skSolve(sketch);
        }
        {
            var Q0;
            Q0=makeQuery(id+"F17.imprint","IMPRINT",FACE,{"disambiguationData":[TD([[makeQuery(id+"F17.imprint","IMPRINT",EDGE,{"derivedFrom":sQuery(id+"F17.wireOp",EDGE,"E34")}),1.0]])]});
            var Q1;
            Q1=sQuery(id+"F17.wireOp",EDGE,"E34");
            extrude(context, id + "F18", {"entities" : qUnion([Q0]), "operationType" : NewBodyOperationType.ADD, "surfaceEntities" : qUnion([Q1]), "depth" : 17 * mm});
        }
        {
            var Q0;
            Q0=qCreatedBy(makeId("Top.planeOp"),FACE);
            var sketch = newSketch(context, id + "F19", { "sketchPlane" : qUnion([Q0])});
            skLineSegment(sketch, "E35.bottom", {"start": v(-35, -69.98) * mm, "end": v(35, -69.98) * mm});
            skLineSegment(sketch, "E35.top", {"start": v(-35, 60.02) * mm, "end": v(35, 60.02) * mm});
            skLineSegment(sketch, "E35.left", {"start": v(-35, -69.98) * mm, "end": v(-35, 60.02) * mm});
            skLineSegment(sketch, "E35.right", {"start": v(35, -69.98) * mm, "end": v(35, 60.02) * mm});
            skLineSegment(sketch, "E36.bottom", {"start": v(-15, 24.03) * mm, "end": v(-11, 24.03) * mm});
            skLineSegment(sketch, "E36.top", {"start": v(-15, -22.9) * mm, "end": v(-11, -22.9) * mm});
            skLineSegment(sketch, "E36.left", {"start": v(-15, 24.03) * mm, "end": v(-15, -22.9) * mm});
            skLineSegment(sketch, "E36.right", {"start": v(-11, 24.03) * mm, "end": v(-11, -22.9) * mm});
            skLineSegment(sketch, "E37.MirrorCS", {"start": v(15, -52.42) * mm, "end": v(11, -52.42) * mm});
            skLineSegment(sketch, "E38.MirrorCS", {"start": v(15, 24.03) * mm, "end": v(11, 24.03) * mm});
            skLineSegment(sketch, "E39.MirrorCS", {"start": v(11, 24.03) * mm, "end": v(11, -52.42) * mm});
            skLineSegment(sketch, "E40.MirrorCS", {"start": v(15, 24.03) * mm, "end": v(15, -52.42) * mm});
            skLineSegment(sketch, "E41.MirrorCS", {"start": v(15, -22.9) * mm, "end": v(11, -22.9) * mm});
            skSolve(sketch);
        }
        {
            var Q0;
            Q0=makeQuery(id+"F19.imprint","IMPRINT",FACE,{"disambiguationData":[TD([[makeQuery(id+"F19.imprint","IMPRINT",EDGE,{"derivedFrom":sQuery(id+"F19.wireOp",EDGE,"E35.bottom")}),1.0]])]});
            var Q1;
            Q1=makeQuery(id+"F19.imprint","IMPRINT",FACE,{"disambiguationData":[TD([[makeQuery(id+"F19.imprint","IMPRINT",EDGE,{"derivedFrom":sQuery(id+"F19.wireOp",EDGE,"E36.bottom")}),-1.0]])]});
            var Q2;
            {var subQ2=sQuery(id+"F19.wireOp",EDGE,"E38.MirrorCS");Q2=makeQuery(id+"F19.imprint","IMPRINT",FACE,{"disambiguationData":[TD([[makeQuery(id+"F19.imprint","IMPRINT",EDGE,{"derivedFrom":subQ2}),1.0]])]});}
            var Q3;
            {var subQ2=sQuery(id+"F19.wireOp",EDGE,"E37.MirrorCS");Q3=makeQuery(id+"F19.imprint","IMPRINT",FACE,{"disambiguationData":[TD([[makeQuery(id+"F19.imprint","IMPRINT",EDGE,{"derivedFrom":subQ2}),-1.0]])]});}
            extrude(context, id + "F20", {"entities" : qUnion([Q0, Q1, Q2, Q3]), "depth" : 5 * mm, "hasDraft" : true, "draftAngle" : 45 * degree, "draftPullDirection" : true});
        }
        {
            var Q0;
            Q0=makeQuery(id+"F20.opExtrude","SWEPT_BODY",BODY,{"disambiguationData":[OSD([sQuery(id+"F19.wireOp",EDGE,"E35.bottom"),sQuery(id+"F19.wireOp",EDGE,"E35.top"),sQuery(id+"F19.wireOp",EDGE,"E35.left"),sQuery(id+"F19.wireOp",EDGE,"E35.right"),sQuery(id+"F19.wireOp",EDGE,"E36.bottom"),sQuery(id+"F19.wireOp",EDGE,"E36.top"),sQuery(id+"F19.wireOp",EDGE,"E36.left"),sQuery(id+"F19.wireOp",EDGE,"E36.right"),sQuery(id+"F19.wireOp",EDGE,"E37.MirrorCS"),sQuery(id+"F19.wireOp",EDGE,"E38.MirrorCS"),sQuery(id+"F19.wireOp",EDGE,"E39.MirrorCS"),sQuery(id+"F19.wireOp",EDGE,"E40.MirrorCS")])]});
            transform(context, id + "F21", {"entities" : qUnion([Q0]), "transformType" : TransformType.TRANSLATION_3D, "dx" : 0 * mm, "dy" : 0 * mm, "dz" : -80 * mm, "makeCopy" : false});
        }
        {
            var Q0;
            Q0=makeQuery(id+"F19.imprint","IMPRINT",FACE,{"disambiguationData":[TD([[makeQuery(id+"F19.imprint","IMPRINT",EDGE,{"derivedFrom":sQuery(id+"F19.wireOp",EDGE,"E36.bottom")}),-1.0]])]});
            var Q1;
            {var subQ2=sQuery(id+"F19.wireOp",EDGE,"E38.MirrorCS");Q1=makeQuery(id+"F19.imprint","IMPRINT",FACE,{"disambiguationData":[TD([[makeQuery(id+"F19.imprint","IMPRINT",EDGE,{"derivedFrom":subQ2}),1.0]])]});}
            extrude(context, id + "F22", {"entities" : qUnion([Q0, Q1]), "oppositeDirection" : true, "depth" : 90 * mm});
        }
        {
            var Q0;
            Q0=makeQuery(id+"F22.opExtrude","SWEPT_BODY",BODY,{"disambiguationData":[OSD([sQuery(id+"F19.wireOp",EDGE,"E36.bottom"),sQuery(id+"F19.wireOp",EDGE,"E36.top"),sQuery(id+"F19.wireOp",EDGE,"E36.left"),sQuery(id+"F19.wireOp",EDGE,"E36.right")])]});
            var Q1;
            Q1=makeQuery(id+"F22.opExtrude","SWEPT_BODY",BODY,{"disambiguationData":[OSD([sQuery(id+"F19.wireOp",EDGE,"E38.MirrorCS"),sQuery(id+"F19.wireOp",EDGE,"E39.MirrorCS"),sQuery(id+"F19.wireOp",EDGE,"E40.MirrorCS"),sQuery(id+"F19.wireOp",EDGE,"E41.MirrorCS")])]});
            transform(context, id + "F23", {"entities" : qUnion([Q0, Q1]), "transformType" : TransformType.TRANSLATION_3D, "dx" : 0 * mm, "dy" : 0 * mm, "dz" : 10 * mm, "makeCopy" : false});
        }
        {
            var Q0;
            Q0=makeQuery(id+"F4.opExtrude","SWEPT_BODY",BODY,{"disambiguationData":[OSD([sQuery(id+"F0.wireOp",EDGE,"E3")])]});
            var Q1;
            Q1=makeQuery(id+"F22.opExtrude","SWEPT_BODY",BODY,{"disambiguationData":[OSD([sQuery(id+"F19.wireOp",EDGE,"E38.MirrorCS"),sQuery(id+"F19.wireOp",EDGE,"E39.MirrorCS"),sQuery(id+"F19.wireOp",EDGE,"E40.MirrorCS"),sQuery(id+"F19.wireOp",EDGE,"E41.MirrorCS")])]});
            var Q2;
            Q2=makeQuery(id+"F22.opExtrude","SWEPT_BODY",BODY,{"disambiguationData":[OSD([sQuery(id+"F19.wireOp",EDGE,"E36.bottom"),sQuery(id+"F19.wireOp",EDGE,"E36.top"),sQuery(id+"F19.wireOp",EDGE,"E36.left"),sQuery(id+"F19.wireOp",EDGE,"E36.right")])]});
            booleanBodies(context, id + "F24", {"operationType" : BooleanOperationType.SUBTRACTION, "tools" : qUnion([Q0]), "targets" : qUnion([Q1, Q2]), "keepTools" : true});
        }
        {
            var Q0;
            Q0=makeQuery(id+"F22.opExtrude","CAP_EDGE",EDGE,{"disambiguationData":[OSD([sQuery(id+"F19.wireOp",EDGE,"E41.MirrorCS")])],"isStart":true});
            var Q1;
            Q1=makeQuery(id+"F22.opExtrude","CAP_EDGE",EDGE,{"disambiguationData":[OSD([sQuery(id+"F19.wireOp",EDGE,"E38.MirrorCS")])],"isStart":true});
            var Q2;
            Q2=makeQuery(id+"F22.opExtrude","CAP_EDGE",EDGE,{"disambiguationData":[OSD([sQuery(id+"F19.wireOp",EDGE,"E36.top")])],"isStart":true});
            var Q3;
            Q3=makeQuery(id+"F22.opExtrude","CAP_EDGE",EDGE,{"disambiguationData":[OSD([sQuery(id+"F19.wireOp",EDGE,"E36.bottom")])],"isStart":true});
            chamfer(context, id + "F25", {"entities" : qUnion([Q0, Q1, Q2, Q3]), "width" : 10 * mm, "tangentPropagation" : true});
        }
        {
            var Q0;
            Q0=makeQuery(id+"F18.opExtrude","CAP_FACE",FACE,{"disambiguationData":[OSD([sQuery(id+"F17.wireOp",EDGE,"E34")])],"isStart":false});
            var sketch = newSketch(context, id + "F26", { "sketchPlane" : qUnion([Q0])});
            skCircle(sketch, "E42", {"center": v(-39.52, 0) * mm, "radius": 1.46 * mm});
            skLineSegment(sketch, "E43.bottom", {"start": v(-39.52, 1.46) * mm, "end": v(-12.25, 1.46) * mm});
            skLineSegment(sketch, "E43.top", {"start": v(-39.52, -1.46) * mm, "end": v(-12.25, -1.46) * mm});
            skLineSegment(sketch, "E43.left", {"start": v(-39.52, 1.46) * mm, "end": v(-39.52, -1.46) * mm});
            skLineSegment(sketch, "E43.right", {"start": v(-12.25, 1.46) * mm, "end": v(-12.25, -1.46) * mm});
            skCircle(sketch, "E44", {"center": v(-12.25, 0) * mm, "radius": 1.46 * mm});
            skSolve(sketch);
        }
        {
            var Q0;
            {var subQ0=sQuery(id+"F26.wireOp",EDGE,"E43.left");Q0=makeQuery(id+"F26.imprint","IMPRINT",FACE,{"disambiguationData":[TD([[makeQuery(id+"F26.imprint","IMPRINT",EDGE,{"derivedFrom":subQ0}),1.0]])]});}
            var Q1;
            {var subQ0=sQuery(id+"F26.wireOp",EDGE,"E43.left");Q1=makeQuery(id+"F26.imprint","IMPRINT",FACE,{"disambiguationData":[TD([[makeQuery(id+"F26.imprint","IMPRINT",EDGE,{"derivedFrom":subQ0}),-1.0]])]});}
            var Q2;
            {var subQ0=makeQuery(id+"F18.opExtrude","CAP_EDGE",EDGE,{"disambiguationData":[OSD([sQuery(id+"F17.wireOp",EDGE,"E34")])],"isStart":false});var subQ3=sQuery(id+"F26.wireOp",EDGE,"E43.bottom");var subQ4=makeQuery(id+"F26.imprint","INTERSECT",VERTEX,{"derivedFrom":[subQ0,subQ3]});Q2=makeQuery(id+"F26.imprint","IMPRINT",FACE,{"disambiguationData":[TD([[makeQuery(id+"F26.imprint","IMPRINT",EDGE,{"disambiguationData":[TD([[subQ4,1.0]])],"derivedFrom":subQ0}),-1.0]])]});}
            var Q3;
            {var subQ0=makeQuery(id+"F18.opExtrude","CAP_EDGE",EDGE,{"disambiguationData":[OSD([sQuery(id+"F17.wireOp",EDGE,"E34")])],"isStart":false});var subQ3=sQuery(id+"F26.wireOp",EDGE,"E43.bottom");var subQ4=makeQuery(id+"F26.imprint","INTERSECT",VERTEX,{"derivedFrom":[subQ0,subQ3]});Q3=makeQuery(id+"F26.imprint","IMPRINT",FACE,{"disambiguationData":[TD([[makeQuery(id+"F26.imprint","IMPRINT",EDGE,{"disambiguationData":[TD([[subQ4,1.0]])],"derivedFrom":subQ0}),1.0]])]});}
            var Q4;
            {var subQ1=sQuery(id+"F26.wireOp",EDGE,"E43.right");Q4=makeQuery(id+"F26.imprint","IMPRINT",FACE,{"disambiguationData":[TD([[makeQuery(id+"F26.imprint","IMPRINT",EDGE,{"derivedFrom":subQ1}),1.0]])]});}
            var Q5;
            {var subQ1=sQuery(id+"F26.wireOp",EDGE,"E43.right");Q5=makeQuery(id+"F26.imprint","IMPRINT",FACE,{"disambiguationData":[TD([[makeQuery(id+"F26.imprint","IMPRINT",EDGE,{"derivedFrom":subQ1}),-1.0]])]});}
            extrude(context, id + "F27", {"entities" : qUnion([Q0, Q1, Q2, Q3, Q4, Q5]), "operationType" : NewBodyOperationType.ADD, "depth" : 2 * mm});
        }
        {
            var Q0;
            {var subQ1=sQuery(id+"F26.wireOp",EDGE,"E43.right");Q0=makeQuery(id+"F26.imprint","IMPRINT",FACE,{"disambiguationData":[TD([[makeQuery(id+"F26.imprint","IMPRINT",EDGE,{"derivedFrom":subQ1}),-1.0]])]});}
            var Q1;
            {var subQ1=sQuery(id+"F26.wireOp",EDGE,"E43.right");Q1=makeQuery(id+"F26.imprint","IMPRINT",FACE,{"disambiguationData":[TD([[makeQuery(id+"F26.imprint","IMPRINT",EDGE,{"derivedFrom":subQ1}),1.0]])]});}
            extrude(context, id + "F28", {"entities" : qUnion([Q0, Q1]), "operationType" : NewBodyOperationType.ADD, "depth" : 15 * mm});
        }
    });
